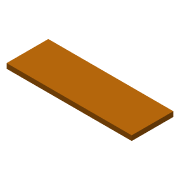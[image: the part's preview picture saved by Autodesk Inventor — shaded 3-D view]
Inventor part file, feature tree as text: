
AUTODESK INVENTOR PART (.ipt)
format: ipt  version: 2014 (Build 180170000, 170)  size: 67,072 bytes
history: native  units: mm
features: extrude x1, sketch x1
ambient origin geometry x8: Origin, YZ Plane, XZ Plane, XY Plane, X Axis, Y Axis, Z Axis, Center Point
bodies: Solid1 (feature_tree)
feature tree (2):
  extrude  "Extrusion1"  Depth=76.2mm
  sketch  "Sketch1"  dims[d0=25.4mm d1=76.2mm d2=3.0mm d3=0.0mm]
